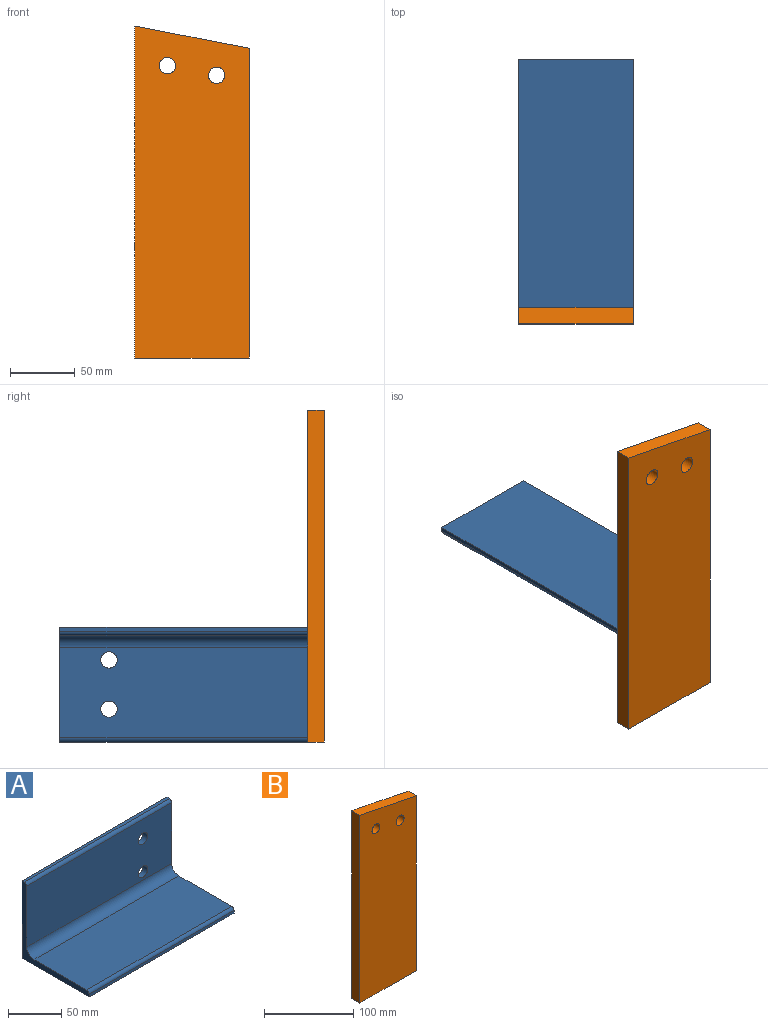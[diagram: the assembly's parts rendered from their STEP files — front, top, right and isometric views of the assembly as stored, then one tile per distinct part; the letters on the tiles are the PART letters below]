
ASSEMBLY  parts=2 mates=1
PART A: 13 faces, bbox 192.1x88.9x88.9 mm
  f0: plane 88.9x88.9mm, normal (1,0,0), area 1103.8mm2, adj f2,f3,f4,f5,f6,f7,f8,f9
  f1: plane 88.9x88.9mm, normal (-1,0,0), area 1103.8mm2, adj f2,f3,f4,f5,f6,f7,f8,f9
  f2: cylinder r=3.17mm len=192.09mm, axis (-1,0,0), area 958mm2, adj f0,f1,f3,f10
  f3: plane 192.09x69.85mm, normal (0,0,1), area 13417.3mm2, adj f0,f1,f2,f4
  f4: cylinder r=9.52mm len=192.09mm, axis (-1,0,0), area 2874mm2, adj f0,f1,f3,f5
  f5: plane 192.09x69.85mm, normal (0,-1,0), area 13164mm2, adj f0,f1,f4,f6,f11,f12
  f6: cylinder r=3.17mm len=192.09mm, axis (-1,0,0), area 958mm2, adj f0,f1,f5,f7
  f7: plane 192.09x3.18mm, normal (0,0,1), area 609.9mm2, adj f0,f1,f6,f8
  f8: plane 192.09x88.9mm, normal (0,1,0), area 16823.2mm2, adj f0,f1,f7,f9,f11,f12
  f9: plane 192.09x88.9mm, normal (0,0,-1), area 17076.6mm2, adj f0,f1,f8,f10
  f10: plane 192.09x3.18mm, normal (0,-1,0), area 609.9mm2, adj f0,f1,f2,f9
  f11: cylinder r=6.35mm len=12.7mm, axis (0,1,0), area 253.4mm2, adj f5,f8
  f12: cylinder r=6.35mm len=12.7mm, axis (0,1,0), area 253.4mm2, adj f5,f8
PART B: 8 faces, bbox 88.9x12.7x257.2 mm
  f0: plane 257.18x12.7mm, normal (-1,0,0), area 3266.1mm2, adj f1,f5,f6,f7
  f1: plane 88.9x12.7mm, normal (0,0,-1), area 1129mm2, adj f0,f2,f6,f7
  f2: plane 239.89x12.7mm, normal (1,0,0), area 3046.7mm2, adj f1,f5,f6,f7
  f3: cylinder r=6.35mm len=12.7mm, axis (0,1,0), area 506.7mm2, adj f6,f7
  f4: cylinder r=6.35mm len=12.7mm, axis (0,1,0), area 506.7mm2, adj f6,f7
  f5: plane 88.9x17.28mm, normal (0.19,0,0.98), area 1150.2mm2, adj f0,f2,f6,f7
  f6: plane 257.18x88.9mm, normal (0,-1,0), area 21841.4mm2, adj f0,f1,f2,f3,f4,f5
  f7: plane 257.18x88.9mm, normal (0,1,0), area 21841.4mm2, adj f0,f1,f2,f3,f4,f5
PLACE A rot(axis=(0.71,0.71,0),180deg) t=(-354.17,382.47,-190.09)mm
PLACE B t=(-398.62,190.38,-150.4)mm
MATE fastened A.f1 <-> B.f7  axis (0,-1,0) through (-398.62,190.38,-190.09)mm
